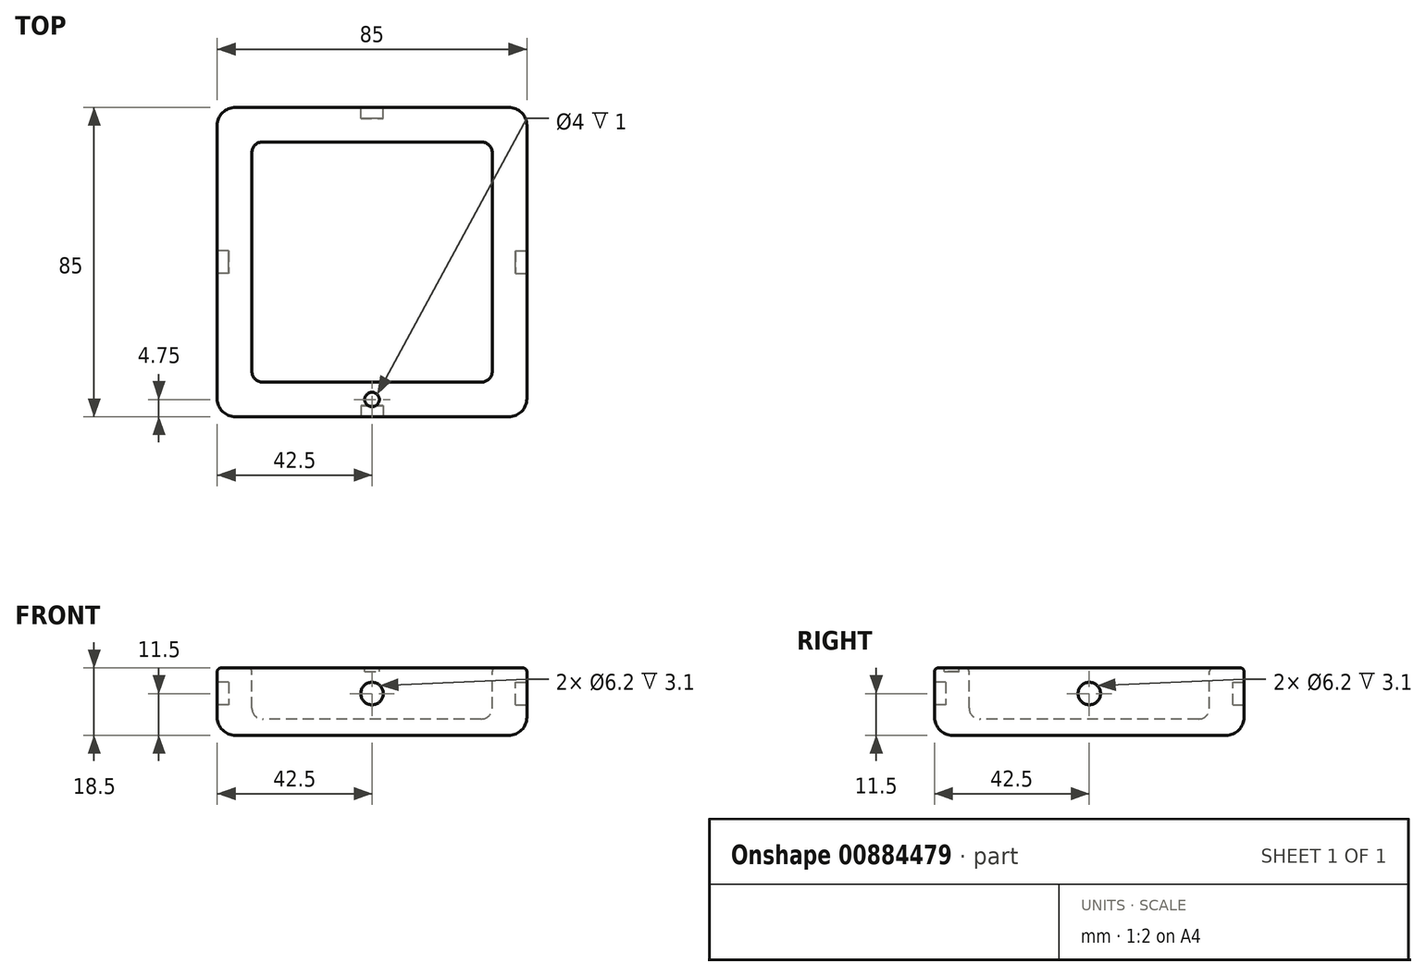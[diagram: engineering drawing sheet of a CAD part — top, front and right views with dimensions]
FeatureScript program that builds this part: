
annotation { "Feature Type Name" : "Feature", "Feature Type Description" : "" }
export const myFeature = defineFeature(function(context is Context, id is Id, definition is map)
    precondition{}
    {
        {
            var Q0;
            Q0=qCreatedBy(makeId("Top.planeOp"),FACE);
            var sketch = newSketch(context, id + "F0", { "sketchPlane" : qUnion([Q0])});
            skLineSegment(sketch, "E0.bottom", {"start": v(-42.5, 42.5) * mm, "end": v(42.5, 42.5) * mm});
            skLineSegment(sketch, "E0.top", {"start": v(-42.5, -42.5) * mm, "end": v(42.5, -42.5) * mm});
            skLineSegment(sketch, "E0.left", {"start": v(-42.5, 42.5) * mm, "end": v(-42.5, -42.5) * mm});
            skLineSegment(sketch, "E0.right", {"start": v(42.5, 42.5) * mm, "end": v(42.5, -42.5) * mm});
            skLineSegment(sketch, "E1.bottom", {"start": v(-30, 33) * mm, "end": v(30, 33) * mm});
            skLineSegment(sketch, "E1.top", {"start": v(-30, -33) * mm, "end": v(30, -33) * mm});
            skLineSegment(sketch, "E1.left", {"start": v(-33, 30) * mm, "end": v(-33, -30) * mm});
            skLineSegment(sketch, "E1.right", {"start": v(33, 30) * mm, "end": v(33, -30) * mm});
            skLineSegment(sketch, "E2.direction1", {"start": v(-33, -33) * mm, "end": v(-8.24, -33) * mm, "construction": true});
            skPoint(sketch, "E3.visualSharp", {"position": v(-33, 33) * mm});
            skArc(sketch, "E3.filletArc", {"start": v(-30, 33) * mm, "mid": v(-32.12, 32.12) * mm, "end": v(-33, 30) * mm});
            skPoint(sketch, "E4.visualSharp", {"position": v(33, 33) * mm});
            skArc(sketch, "E4.filletArc", {"start": v(33, 30) * mm, "mid": v(32.12, 32.12) * mm, "end": v(30, 33) * mm});
            skPoint(sketch, "E5.visualSharp", {"position": v(33, -33) * mm});
            skArc(sketch, "E5.filletArc", {"start": v(30, -33) * mm, "mid": v(32.12, -32.12) * mm, "end": v(33, -30) * mm});
            skPoint(sketch, "E6.visualSharp", {"position": v(-33, -33) * mm});
            skArc(sketch, "E6.filletArc", {"start": v(-33, -30) * mm, "mid": v(-32.12, -32.12) * mm, "end": v(-30, -33) * mm});
            skLineSegment(sketch, "E7.direction1", {"start": v(-33, -33) * mm, "end": v(-6.5, -33) * mm, "construction": true});
            skLineSegment(sketch, "E8", {"start": v(-42.5, 0) * mm, "end": v(42.5, 0) * mm, "construction": true});
            skLineSegment(sketch, "E9", {"start": v(0, -42.5) * mm, "end": v(0, 42.5) * mm, "construction": true});
            skCircle(sketch, "E10", {"center": v(0, -37.75) * mm, "radius": 2 * mm});
            skSolve(sketch);
        }
        {
            assignVariable(context, id + "F1", {"name" : "h", "anyValue" : 18.5});
        }
        {
            assignVariable(context, id + "F2", {"name" : "d", "anyValue" : 14});
        }
        {
            var Q0;
            Q0=makeQuery(id+"F0.imprint","IMPRINT",FACE,{"disambiguationData":[TD([[makeQuery(id+"F0.imprint","IMPRINT",EDGE,{"derivedFrom":sQuery(id+"F0.wireOp",EDGE,"E1.bottom")}),-1.0]])]});
            var Q1;
            Q1=makeQuery(id+"F0.imprint","IMPRINT",FACE,{"disambiguationData":[TD([[makeQuery(id+"F0.imprint","IMPRINT",EDGE,{"derivedFrom":sQuery(id+"F0.wireOp",EDGE,"E0.bottom")}),-1.0]])]});
            var Q2;
            Q2=makeQuery(id+"F0.imprint","IMPRINT",FACE,{"disambiguationData":[TD([[makeQuery(id+"F0.imprint","IMPRINT",EDGE,{"derivedFrom":sQuery(id+"F0.wireOp",EDGE,"E2.0.2.0")}),1.0]])]});
            var Q3;
            Q3=makeQuery(id+"F0.imprint","IMPRINT",FACE,{"disambiguationData":[TD([[makeQuery(id+"F0.imprint","IMPRINT",EDGE,{"derivedFrom":sQuery(id+"F0.wireOp",EDGE,"E2.0.3.0")}),1.0]])]});
            var Q4;
            Q4=makeQuery(id+"F0.imprint","IMPRINT",FACE,{"disambiguationData":[TD([[makeQuery(id+"F0.imprint","IMPRINT",EDGE,{"derivedFrom":sQuery(id+"F0.wireOp",EDGE,"E2.0.1.0")}),1.0]])]});
            var Q5;
            Q5=makeQuery(id+"F0.imprint","IMPRINT",FACE,{"disambiguationData":[TD([[makeQuery(id+"F0.imprint","IMPRINT",EDGE,{"derivedFrom":sQuery(id+"F0.wireOp",EDGE,"E7.0.1.2")}),1.0]])]});
            var Q6;
            Q6=makeQuery(id+"F0.imprint","IMPRINT",FACE,{"disambiguationData":[TD([[makeQuery(id+"F0.imprint","IMPRINT",EDGE,{"derivedFrom":sQuery(id+"F0.wireOp",EDGE,"E7.0.2.2")}),1.0]])]});
            var Q7;
            Q7=makeQuery(id+"F0.imprint","IMPRINT",FACE,{"disambiguationData":[TD([[makeQuery(id+"F0.imprint","IMPRINT",EDGE,{"derivedFrom":sQuery(id+"F0.wireOp",EDGE,"E7.0.3.2")}),1.0]])]});
            var Q8;
            Q8=makeQuery(id+"F0.imprint","IMPRINT",FACE,{"disambiguationData":[TD([[makeQuery(id+"F0.imprint","IMPRINT",EDGE,{"derivedFrom":sQuery(id+"F0.wireOp",EDGE,"E10")}),1.0]])]});
            extrude(context, id + "F3", {"entities" : qUnion([Q0, Q1, Q2, Q3, Q4, Q5, Q6, Q7, Q8]), "depth" : (getVariable(context, 'h')) * mm, "offsetDistance" : 25 * mm});
        }
        {
            var Q0;
            Q0=makeQuery(id+"F0.imprint","IMPRINT",FACE,{"disambiguationData":[TD([[makeQuery(id+"F0.imprint","IMPRINT",EDGE,{"derivedFrom":sQuery(id+"F0.wireOp",EDGE,"E1.bottom")}),-1.0]])]});
            var Q1;
            Q1=makeQuery(id+"F0.imprint","IMPRINT",FACE,{"disambiguationData":[TD([[makeQuery(id+"F0.imprint","IMPRINT",EDGE,{"derivedFrom":sQuery(id+"F0.wireOp",EDGE,"E2.0.1.0")}),1.0]])]});
            var Q2;
            Q2=makeQuery(id+"F0.imprint","IMPRINT",FACE,{"disambiguationData":[TD([[makeQuery(id+"F0.imprint","IMPRINT",EDGE,{"derivedFrom":sQuery(id+"F0.wireOp",EDGE,"E2.0.2.0")}),1.0]])]});
            var Q3;
            Q3=makeQuery(id+"F0.imprint","IMPRINT",FACE,{"disambiguationData":[TD([[makeQuery(id+"F0.imprint","IMPRINT",EDGE,{"derivedFrom":sQuery(id+"F0.wireOp",EDGE,"E2.0.3.0")}),1.0]])]});
            var Q4;
            Q4=makeQuery(id+"F0.imprint","IMPRINT",FACE,{"disambiguationData":[TD([[makeQuery(id+"F0.imprint","IMPRINT",EDGE,{"derivedFrom":sQuery(id+"F0.wireOp",EDGE,"E7.0.1.2")}),1.0]])]});
            var Q5;
            Q5=makeQuery(id+"F0.imprint","IMPRINT",FACE,{"disambiguationData":[TD([[makeQuery(id+"F0.imprint","IMPRINT",EDGE,{"derivedFrom":sQuery(id+"F0.wireOp",EDGE,"E7.0.2.2")}),1.0]])]});
            var Q6;
            Q6=makeQuery(id+"F0.imprint","IMPRINT",FACE,{"disambiguationData":[TD([[makeQuery(id+"F0.imprint","IMPRINT",EDGE,{"derivedFrom":sQuery(id+"F0.wireOp",EDGE,"E7.0.3.2")}),1.0]])]});
            extrude(context, id + "F4", {"entities" : qUnion([Q0, Q1, Q2, Q3, Q4, Q5, Q6]), "operationType" : NewBodyOperationType.REMOVE, "depth" : (getVariable(context, 'd')) * mm, "offsetDistance" : 25 * mm});
        }
        {
            var Q0;
            Q0=makeQuery(id+"F3.opExtrude","CAP_FACE",FACE,{"disambiguationData":[OSD([sQuery(id+"F0.wireOp",EDGE,"E0.bottom"),sQuery(id+"F0.wireOp",EDGE,"E0.top"),sQuery(id+"F0.wireOp",EDGE,"E0.left"),sQuery(id+"F0.wireOp",EDGE,"E0.right")])],"isStart":false});
            var Q1;
            Q1=makeQuery(id+"F3.opExtrude","SWEPT_EDGE",EDGE,{"disambiguationData":[OSD([sQuery(id+"F0.wireOp",EDGE,"E0.bottom"),sQuery(id+"F0.wireOp",EDGE,"E0.right")])]});
            var Q2;
            Q2=makeQuery(id+"F3.opExtrude","SWEPT_EDGE",EDGE,{"disambiguationData":[OSD([sQuery(id+"F0.wireOp",EDGE,"E0.bottom"),sQuery(id+"F0.wireOp",EDGE,"E0.left")])]});
            var Q3;
            Q3=makeQuery(id+"F3.opExtrude","SWEPT_EDGE",EDGE,{"disambiguationData":[OSD([sQuery(id+"F0.wireOp",EDGE,"E0.top"),sQuery(id+"F0.wireOp",EDGE,"E0.left")])]});
            var Q4;
            Q4=makeQuery(id+"F3.opExtrude","SWEPT_EDGE",EDGE,{"disambiguationData":[OSD([sQuery(id+"F0.wireOp",EDGE,"E0.top"),sQuery(id+"F0.wireOp",EDGE,"E0.right")])]});
            fillet(context, id + "F5", {"entities" : qUnion([Q0, Q1, Q2, Q3, Q4]), "radius" : 5 * mm, "tangentPropagation" : true, "allowEdgeOverflow" : false});
        }
        {
            var Q0;
            Q0=makeQuery(id+"F4.boolean.opBoolean","COPY",FACE,{"derivedFrom":makeQuery(id+"F4.opExtrude","CAP_FACE",FACE,{"disambiguationData":[OSD([sQuery(id+"F0.wireOp",EDGE,"E1.bottom"),sQuery(id+"F0.wireOp",EDGE,"E1.top"),sQuery(id+"F0.wireOp",EDGE,"E1.left"),sQuery(id+"F0.wireOp",EDGE,"E1.right"),sQuery(id+"F0.wireOp",EDGE,"E3.filletArc"),sQuery(id+"F0.wireOp",EDGE,"E4.filletArc"),sQuery(id+"F0.wireOp",EDGE,"E5.filletArc"),sQuery(id+"F0.wireOp",EDGE,"E6.filletArc")])],"isStart":false})});
            var Q1;
            Q1=makeQuery(id+"F4.boolean.opBoolean","COPY",FACE,{"derivedFrom":makeQuery(id+"F4.opExtrude","CAP_FACE",FACE,{"disambiguationData":[OSD([sQuery(id+"F0.wireOp",EDGE,"E7.0.1.2"),sQuery(id+"F0.wireOp",EDGE,"E7.0.1.4"),sQuery(id+"F0.wireOp",EDGE,"E7.0.1.5"),sQuery(id+"F0.wireOp",EDGE,"E7.0.1.6"),sQuery(id+"F0.wireOp",EDGE,"E7.0.1.7"),sQuery(id+"F0.wireOp",EDGE,"E7.0.1.9"),sQuery(id+"F0.wireOp",EDGE,"E7.0.1.11"),sQuery(id+"F0.wireOp",EDGE,"E7.0.1.12")])],"isStart":false})});
            var Q2;
            Q2=makeQuery(id+"F4.boolean.opBoolean","COPY",FACE,{"derivedFrom":makeQuery(id+"F4.opExtrude","CAP_FACE",FACE,{"disambiguationData":[OSD([sQuery(id+"F0.wireOp",EDGE,"E7.0.2.2"),sQuery(id+"F0.wireOp",EDGE,"E7.0.2.4"),sQuery(id+"F0.wireOp",EDGE,"E7.0.2.5"),sQuery(id+"F0.wireOp",EDGE,"E7.0.2.6"),sQuery(id+"F0.wireOp",EDGE,"E7.0.2.7"),sQuery(id+"F0.wireOp",EDGE,"E7.0.2.9"),sQuery(id+"F0.wireOp",EDGE,"E7.0.2.11"),sQuery(id+"F0.wireOp",EDGE,"E7.0.2.12")])],"isStart":false})});
            var Q3;
            Q3=makeQuery(id+"F4.boolean.opBoolean","COPY",FACE,{"derivedFrom":makeQuery(id+"F4.opExtrude","CAP_FACE",FACE,{"disambiguationData":[OSD([sQuery(id+"F0.wireOp",EDGE,"E7.0.3.2"),sQuery(id+"F0.wireOp",EDGE,"E7.0.3.4"),sQuery(id+"F0.wireOp",EDGE,"E7.0.3.5"),sQuery(id+"F0.wireOp",EDGE,"E7.0.3.6"),sQuery(id+"F0.wireOp",EDGE,"E7.0.3.7"),sQuery(id+"F0.wireOp",EDGE,"E7.0.3.9"),sQuery(id+"F0.wireOp",EDGE,"E7.0.3.11"),sQuery(id+"F0.wireOp",EDGE,"E7.0.3.12")])],"isStart":false})});
            fillet(context, id + "F6", {"entities" : qUnion([Q0, Q1, Q2, Q3]), "radius" : 3 * mm, "tangentPropagation" : true, "allowEdgeOverflow" : false});
        }
        {
            var Q0;
            Q0=makeQuery(id+"F3.opExtrude","CAP_FACE",FACE,{"disambiguationData":[OSD([sQuery(id+"F0.wireOp",EDGE,"E0.bottom"),sQuery(id+"F0.wireOp",EDGE,"E0.top"),sQuery(id+"F0.wireOp",EDGE,"E0.left"),sQuery(id+"F0.wireOp",EDGE,"E0.right")])],"isStart":true});
            fillet(context, id + "F7", {"entities" : qUnion([Q0]), "radius" : 1 * mm, "tangentPropagation" : true, "allowEdgeOverflow" : false});
        }
        {
            var Q0;
            Q0=makeQuery(id+"F3.opExtrude","SWEPT_FACE",FACE,{"disambiguationData":[OSD([sQuery(id+"F0.wireOp",EDGE,"E0.top")])]});
            var sketch = newSketch(context, id + "F8", { "sketchPlane" : qUnion([Q0])});
            skCircle(sketch, "E11", {"center": v(0, 7) * mm, "radius": 3.1 * mm});
            skSolve(sketch);
        }
        {
            var Q0;
            Q0=makeQuery(id+"F8.imprint","IMPRINT",FACE,{"disambiguationData":[TD([[makeQuery(id+"F8.imprint","IMPRINT",EDGE,{"derivedFrom":sQuery(id+"F8.wireOp",EDGE,"E11")}),1.0]])]});
            extrude(context, id + "F9", {"entities" : qUnion([Q0]), "operationType" : NewBodyOperationType.REMOVE, "oppositeDirection" : true, "depth" : 3.1 * mm, "offsetDistance" : 25 * mm});
        }
        {
            var Q0;
            Q0=makeQuery(id+"F3.opExtrude","SWEPT_FACE",FACE,{"disambiguationData":[OSD([sQuery(id+"F0.wireOp",EDGE,"E0.bottom")])]});
            var sketch = newSketch(context, id + "F10", { "sketchPlane" : qUnion([Q0])});
            skCircle(sketch, "E12", {"center": v(0, 7) * mm, "radius": 3.1 * mm});
            skSolve(sketch);
        }
        {
            var Q0;
            Q0=makeQuery(id+"F10.imprint","IMPRINT",FACE,{"disambiguationData":[TD([[makeQuery(id+"F10.imprint","IMPRINT",EDGE,{"derivedFrom":sQuery(id+"F10.wireOp",EDGE,"E12")}),1.0]])]});
            extrude(context, id + "F11", {"entities" : qUnion([Q0]), "operationType" : NewBodyOperationType.REMOVE, "oppositeDirection" : true, "depth" : 3.1 * mm, "offsetDistance" : 25 * mm});
        }
        {
            var Q0;
            Q0=makeQuery(id+"F3.opExtrude","SWEPT_FACE",FACE,{"disambiguationData":[OSD([sQuery(id+"F0.wireOp",EDGE,"E0.left")])]});
            var sketch = newSketch(context, id + "F12", { "sketchPlane" : qUnion([Q0])});
            skCircle(sketch, "E13", {"center": v(0, 7) * mm, "radius": 3.1 * mm});
            skSolve(sketch);
        }
        {
            var Q0;
            Q0=makeQuery(id+"F12.imprint","IMPRINT",FACE,{"disambiguationData":[TD([[makeQuery(id+"F12.imprint","IMPRINT",EDGE,{"derivedFrom":sQuery(id+"F12.wireOp",EDGE,"E13")}),1.0]])]});
            extrude(context, id + "F13", {"entities" : qUnion([Q0]), "operationType" : NewBodyOperationType.REMOVE, "oppositeDirection" : true, "depth" : 3.1 * mm, "offsetDistance" : 25 * mm});
        }
        {
            var Q0;
            Q0=makeQuery(id+"F3.opExtrude","SWEPT_FACE",FACE,{"disambiguationData":[OSD([sQuery(id+"F0.wireOp",EDGE,"E0.right")])]});
            var sketch = newSketch(context, id + "F14", { "sketchPlane" : qUnion([Q0])});
            skCircle(sketch, "E14", {"center": v(0, 7) * mm, "radius": 3.1 * mm});
            skSolve(sketch);
        }
        {
            var Q0;
            Q0=makeQuery(id+"F14.imprint","IMPRINT",FACE,{"disambiguationData":[TD([[makeQuery(id+"F14.imprint","IMPRINT",EDGE,{"derivedFrom":sQuery(id+"F14.wireOp",EDGE,"E14")}),1.0]])]});
            extrude(context, id + "F15", {"entities" : qUnion([Q0]), "operationType" : NewBodyOperationType.REMOVE, "oppositeDirection" : true, "depth" : 3.1 * mm, "offsetDistance" : 25 * mm});
        }
        {
            var Q0;
            Q0=makeQuery(id+"F0.imprint","IMPRINT",FACE,{"disambiguationData":[TD([[makeQuery(id+"F0.imprint","IMPRINT",EDGE,{"derivedFrom":sQuery(id+"F0.wireOp",EDGE,"E10")}),1.0]])]});
            var Q1;
            Q1=sQuery(id+"F0.wireOp",EDGE,"E10");
            extrude(context, id + "F16", {"entities" : qUnion([Q0]), "operationType" : NewBodyOperationType.REMOVE, "surfaceEntities" : qUnion([Q1]), "depth" : 1 * mm, "offsetDistance" : 25 * mm});
        }
        {
            var Q0;
            Q0=makeQuery(id+"F3.opExtrude","SWEPT_BODY",BODY,{"disambiguationData":[OSD([sQuery(id+"F0.wireOp",EDGE,"E0.bottom"),sQuery(id+"F0.wireOp",EDGE,"E0.top"),sQuery(id+"F0.wireOp",EDGE,"E0.left"),sQuery(id+"F0.wireOp",EDGE,"E0.right")])]});
            var Q1;
            Q1=sQuery(id+"F0.wireOp",EDGE,"E9");
            var Q2;
            Q2=sQuery(id+"F0.wireOp",EDGE,"E9");
            transform(context, id + "F17", {"entities" : qUnion([Q0]), "transformType" : TransformType.ROTATION, "transformAxis" : qUnion([Q2]), "angle" : 180 * degree, "makeCopy" : false});
        }
    });
